# Revit family: ITK _Переходник
name_source: partatom
category: Обобщенные модели
units: mm (PartAtom-declared; Revit-internal decimal feet)

## family parameters
Всегда вертикально = Да
Может служить основой для арматурных стержней = Нет
На основе рабочей плоскости = Нет
Общий = Нет
При загрузке вырезать с полостями = Нет
Размер круглого соединителя = Использовать диаметр
Тип детали = Нормальный
Точка расчета площади = Нет

## types (1)
- AD35-01U
    ADSK_URL страницы изделия = https://www.itk-group.ru
    ADSK_Версия Revit = 2019
    ADSK_Версия семейства = 1.0
    ADSK_Группирование = I. ЩИТЫ И ПУЛЬТЫ
    ADSK_Единица измерения = шт
    ADSK_Завод-изготовитель = IEK
    ADSK_Код изделия = AD35-01U
    ADSK_Масса = 0.05
    ADSK_Материал наименование = Сталь
    ADSK_Наименование = ITK Переходник с 19" на 21", 1U, серый
    IEK_URL = https://www.itk-group.ru
    IEK_Описание = Совместимы со всеми 21" шкафами и стойками.
Удобны в монтаже и эксплуатации.
Монтаж с использованием крепежа винт-шайба-гайка М6.
Соответствие российским и международным стандартам.
Поставляются в полиэтиленовом пакете.
    IEK_Цена за единицу = 768.4
    KSI_CMa_Строительные материалы = 10.03.02.06
    KSI_CPr_Строительные изделия = 61.1.03.04
    URL = https://www.iek.ru
    Изготовитель = ITK
    Тип монтажа = Навесной
